# Revit family: CPFB_CW_DBD
name_source: partatom
category: Mechanical Equipment
units: mm (PartAtom-declared; Revit-internal decimal feet)

## family parameters
Always vertical = Yes
Cut with Voids When Loaded = No
Part Type = Normal
Room Calculation Point = No
Round Connector Dimension = Use Radius
Shared = No
Work Plane-Based = No

## types (8) — shared parameters
-.125 = -0' - 0 1/8"
-1.5 = -0' - 1 1/2"
0 = 0' - 0"
1'8" = 1' - 8"
1.5 = 0' - 1 1/2"
4" = 0' - 4"
Manufacturer = Loren Cook Company
Model = CPFB_CW_DBD
ONE EIGTH = 0' - 0 1/8"
Type Comments = Foward Curved Centrifugal Blower Clockwise Downblast Arrangement 10
URL = www.lorencook.com

## per-type parameters (varying)
- 150-CPFB_CW_DBD: (C/2)-.25=0' - 9 5/16"; (C/2)-1.5=0' - 8 1/16"; -(A+.25)=-0' - 11 9/16"; A=0' - 11 7/16"; A+.25=0' - 11 9/16"; B=1' - 4 7/16"; C=1' - 7 1/8"; C/2=0' - 9 9/16"; C/8=0' - 3 3/16"; C/8*7=0' - 5 31/32"; CUT=0' - 2"; D=1' - 7 1/16"; E=2' - 4 1/2"; E-U=2' - 0 3/4"; F=1' - 0 3/16"; F-.125=1' - 0 1/16"; G=0' - 9 3/8"; G-V=0' - 1 3/8"; H=2' - 5 1/16"; J=1' - 2 5/8"; K=1' - 0"; L=1' - 2 1/8"; M=1' - 3 1/8"; N=1' - 1 1/4"; P=2' - 9 5/16"; P-U=2' - 5 9/16"; Q=0' - 3"; R=0' - 0 3/4"; S=0' - 0 9/16"; S/2=0' - 0 9/32"; T=0' - 0 3/4"; U=0' - 3 3/4"; U-.125=0' - 3 5/8"; V=0' - 8"; W=0' - 4"; W+1.5=0' - 5 1/2"; W+1.5+K+L=2' - 7 5/8"; W+M=1' - 7 1/8"; X=1' - 7 5/8"; Y=0' - 8 5/8"; Z=0' - 6 9/16"
- 180-CPFB_CW_DBD: (C/2)-.25=0' - 11 3/32"; (C/2)-1.5=0' - 9 27/32"; -(A+.25)=-1' - 1 7/8"; A=1' - 1 3/4"; A+.25=1' - 1 7/8"; B=1' - 7 11/16"; C=1' - 10 11/16"; C/2=0' - 11 11/32"; C/8=0' - 3 25/32"; C/8*7=0' - 7 3/32"; CUT=0' - 2"; D=1' - 10 1/16"; E=2' - 10 3/16"; E-U=2' - 5 3/4"; F=1' - 2 5/8"; F-.125=1' - 2 1/2"; G=0' - 10 3/8"; G-V=0' - 1 3/8"; H=2' - 9 9/16"; J=1' - 4 15/16"; K=1' - 0"; L=1' - 4 7/16"; M=1' - 3 1/8"; N=1' - 3 9/16"; P=3' - 3 3/16"; P-U=2' - 10 3/4"; Q=0' - 3"; R=0' - 1"; S=0' - 0 9/16"; S/2=0' - 0 9/32"; T=0' - 0 3/4"; U=0' - 4 7/16"; U-.125=0' - 4 5/16"; V=0' - 9"; W=0' - 4"; W+1.5=0' - 5 1/2"; W+1.5+K+L=2' - 9 15/16"; W+M=1' - 7 1/8"; X=1' - 10 7/8"; Y=0' - 9 5/8"; Z=0' - 7 3/4"
- 220-CPFB_CW_DBD: (C/2)-.25=1' - 1 15/32"; (C/2)-1.5=1' - 0 7/32"; -(A+.25)=-1' - 5 5/16"; A=1' - 5 3/16"; A+.25=1' - 5 5/16"; B=2' - 0 5/8"; C=2' - 3 7/16"; C/2=1' - 1 23/32"; C/8=0' - 4 9/16"; C/8*7=0' - 8 9/16"; CUT=0' - 2"; D=2' - 3"; E=3' - 6 3/4"; E-U=3' - 0 3/8"; F=1' - 6 5/16"; F-.125=1' - 6 3/16"; G=0' - 11 7/8"; G-V=0' - 1 3/8"; H=3' - 5"; J=1' - 8 7/16"; K=1' - 3"; L=1' - 7 7/8"; M=1' - 6 1/8"; N=1' - 7"; P=4' - 0 3/8"; P-U=3' - 6"; Q=0' - 4"; R=0' - 1"; S=0' - 0 9/16"; S/2=0' - 0 9/32"; T=0' - 0 3/4"; U=0' - 6 3/8"; U-.125=0' - 6 1/4"; V=0' - 10 1/2"; W=0' - 5"; W+1.5=0' - 6 1/2"; W+1.5+K+L=3' - 5 3/8"; W+M=1' - 11 1/8"; X=2' - 3 13/16"; Y=0' - 11 1/8"; Z=0' - 9 7/16"
- 250-CPFB_CW_DBD: (C/2)-.25=1' - 2 15/32"; (C/2)-1.5=1' - 1 7/32"; -(A+.25)=-1' - 6 7/8"; A=1' - 6 3/4"; A+.25=1' - 6 7/8"; B=2' - 2 13/16"; C=2' - 5 7/16"; C/2=1' - 2 23/32"; C/8=0' - 4 29/32"; C/8*7=0' - 9 3/16"; CUT=0' - 2"; D=2' - 5 5/8"; E=3' - 10 1/2"; E-U=3' - 2 5/8"; F=1' - 7 7/8"; F-.125=1' - 7 3/4"; G=1' - 1 3/8"; G-V=0' - 1 7/8"; H=3' - 8 5/8"; J=1' - 11"; K=1' - 3"; L=1' - 9 11/16"; M=1' - 6 1/8"; N=1' - 9 1/16"; P=4' - 4 15/16"; P-U=3' - 9 1/16"; Q=0' - 4"; R=0' - 1"; S=0' - 0 11/16"; S/2=0' - 0 11/32"; T=0' - 1"; U=0' - 7 7/8"; U-.125=0' - 7 3/4"; V=0' - 11 1/2"; W=0' - 5"; W+1.5=0' - 6 1/2"; W+1.5+K+L=3' - 7 3/16"; W+M=1' - 11 1/8"; X=2' - 7"; Y=1' - 0 3/8"; Z=0' - 10 1/2"
- 270-CPFB_CW_DBD: (C/2)-.25=1' - 3 23/32"; (C/2)-1.5=1' - 2 15/32"; -(A+.25)=-1' - 8 3/4"; A=1' - 8 5/8"; A+.25=1' - 8 3/4"; B=2' - 5 9/16"; C=2' - 7 15/16"; C/2=1' - 3 31/32"; C/8=0' - 5 5/16"; C/8*7=0' - 9 31/32"; CUT=0' - 2 1/4"; D=2' - 8 3/8"; E=4' - 3 5/16"; E-U=3' - 6 5/16"; F=1' - 10 1/16"; F-.125=1' - 9 15/16"; G=1' - 2 3/8"; G-V=0' - 1 7/8"; H=4' - 0 7/8"; J=2' - 0 7/8"; K=1' - 6"; L=1' - 11 9/16"; M=1' - 9 1/8"; N=1' - 10 15/16"; P=4' - 10 1/16"; P-U=4' - 1 1/16"; Q=0' - 4"; R=0' - 1"; S=0' - 0 11/16"; S/2=0' - 0 11/32"; T=0' - 1"; U=0' - 9"; U-.125=0' - 8 7/8"; V=1' - 0 1/2"; W=0' - 5"; W+1.5=0' - 6 1/2"; W+1.5+K+L=4' - 0 1/16"; W+M=2' - 2 1/8"; X=2' - 9 3/4"; Y=1' - 1 3/8"; Z=0' - 11 7/16"
- 300-CPFB_CW_DBD: (C/2)-.25=1' - 5 7/32"; (C/2)-1.5=1' - 3 31/32"; -(A+.25)=-1' - 11 1/16"; A=1' - 10 15/16"; A+.25=1' - 11 1/16"; B=2' - 8 13/16"; C=2' - 10 15/16"; C/2=1' - 5 15/32"; C/8=0' - 5 13/16"; C/8*7=0' - 10 29/32"; CUT=0' - 2 1/2"; D=2' - 11 5/8"; E=4' - 9"; E-U=3' - 11 1/4"; F=2' - 0 3/8"; F-.125=2' - 0 1/4"; G=1' - 3 5/16"; G-V=0' - 1 13/16"; H=4' - 5 5/8"; J=2' - 3 3/16"; K=1' - 6"; L=2' - 2"; M=1' - 9 3/16"; N=2' - 1 5/16"; P=5' - 4 1/8"; P-U=4' - 6 3/8"; Q=0' - 4"; R=0' - 1 3/16"; S=0' - 0 11/16"; S/2=0' - 0 11/32"; T=0' - 1"; U=0' - 9 3/4"; U-.125=0' - 9 5/8"; V=1' - 1 1/2"; W=0' - 5"; W+1.5=0' - 6 1/2"; W+1.5+K+L=4' - 2 1/2"; W+M=2' - 2 3/16"; X=3' - 1"; Y=1' - 2 5/16"; Z=1' - 0 5/8"
- 120-CPFB_CW_DBD: (C/2)-.25=0' - 7 13/16"; (C/2)-1.5=0' - 6 9/16"; -(A+.25)=-0' - 9 5/16"; A=0' - 9 3/16"; A+.25=0' - 9 5/16"; B=1' - 1 1/8"; C=1' - 4 1/8"; C/2=0' - 8 1/16"; C/8=0' - 2 11/16"; C/8*7=0' - 5 1/32"; CUT=0' - 2 1/2"; D=1' - 6"; E=1' - 10 13/16"; E-U=1' - 6 3/16"; F=0' - 9 3/4"; F-.125=0' - 9 5/8"; G=0' - 9 3/8"; G-V=0' - 1 3/8"; H=2' - 2 1/4"; J=1' - 0 3/8"; K=0' - 10"; L=0' - 11 7/8"; M=1' - 1 1/8"; N=0' - 11"; P=2' - 5 7/16"; P-U=2' - 0 13/16"; Q=0' - 3"; R=0' - 0 3/4"; S=0' - 0 9/16"; S/2=0' - 0 9/32"; T=0' - 0 3/4"; U=0' - 4 5/8"; U-.125=0' - 4 1/2"; V=0' - 8"; W=0' - 4"; W+1.5=0' - 5 1/2"; W+1.5+K+L=2' - 3 3/8"; W+M=1' - 5 1/8"; X=1' - 4 5/16"; Y=0' - 8 5/8"; Z=0' - 5 7/16"
- 100-CPFB_CW_DBD: (C/2)-.25=0' - 6 13/16"; (C/2)-1.5=0' - 5 9/16"; -(A+.25)=-0' - 7 11/16"; A=0' - 7 9/16"; A+.25=0' - 7 11/16"; B=0' - 10 15/16"; C=1' - 2 1/8"; C/2=0' - 7 1/16"; C/8=0' - 2 11/32"; C/8*7=0' - 4 13/32"; CUT=0' - 3 1/2"; D=1' - 6"; E=1' - 7"; E-U=1' - 1 3/4"; F=0' - 8 1/8"; F-.125=0' - 8"; G=0' - 9 3/8"; G-V=0' - 1 3/8"; H=2' - 1 1/4"; J=0' - 10 3/4"; K=0' - 10"; L=0' - 10 1/4"; M=1' - 1 1/8"; N=0' - 9 3/8"; P=2' - 3 1/2"; P-U=1' - 10 1/4"; Q=0' - 3"; R=0' - 0 3/4"; S=0' - 0 9/16"; S/2=0' - 0 9/32"; T=0' - 0 3/4"; U=0' - 5 1/4"; U-.125=0' - 5 1/8"; V=0' - 8"; W=0' - 4"; W+1.5=0' - 5 1/2"; W+1.5+K+L=2' - 1 3/4"; W+M=1' - 5 1/8"; X=1' - 2 1/16"; Y=0' - 8 5/8"; Z=0' - 4 5/8"

## geometry (parser evidence)
native form markers: Sweep x2
no freeform markers — native parametric forms only
